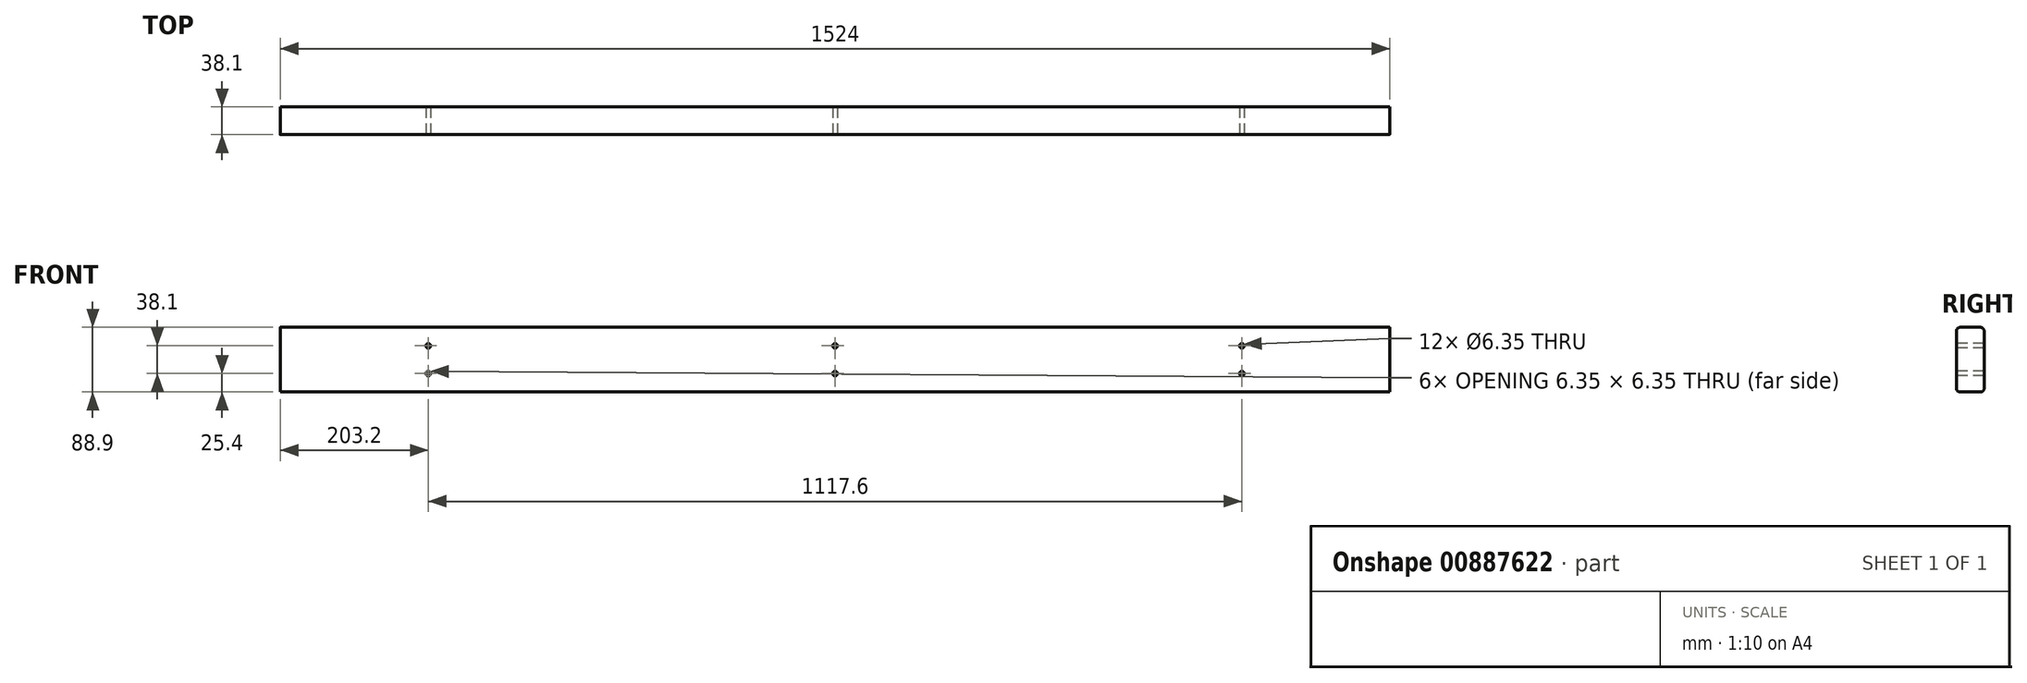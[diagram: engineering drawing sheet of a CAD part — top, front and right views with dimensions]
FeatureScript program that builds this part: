
annotation { "Feature Type Name" : "Feature", "Feature Type Description" : "" }
export const myFeature = defineFeature(function(context is Context, id is Id, definition is map)
    precondition{}
    {
        {
            var Q0;
            Q0=qCreatedBy(makeId("Right.planeOp"),FACE);
            var sketch = newSketch(context, id + "F0", { "sketchPlane" : qUnion([Q0])});
            skLineSegment(sketch, "E0.bottom", {"start": v(19.05, 44.45) * mm, "end": v(-19.05, 44.45) * mm});
            skLineSegment(sketch, "E0.top", {"start": v(19.05, -44.45) * mm, "end": v(-19.05, -44.45) * mm});
            skLineSegment(sketch, "E0.left", {"start": v(19.05, 44.45) * mm, "end": v(19.05, -44.45) * mm});
            skLineSegment(sketch, "E0.right", {"start": v(-19.05, 44.45) * mm, "end": v(-19.05, -44.45) * mm});
            skPoint(sketch, "E0.middle", {"position": v(0, 0) * mm});
            skSolve(sketch);
        }
        {
            var Q0;
            Q0=makeQuery(id+"F0.imprint","IMPRINT",FACE,{"disambiguationData":[TD([[makeQuery(id+"F0.imprint","IMPRINT",EDGE,{"derivedFrom":sQuery(id+"F0.wireOp",EDGE,"E0.bottom")}),1.0]])]});
            extrude(context, id + "F1", {"entities" : qUnion([Q0]), "endBound" : BoundingType.SYMMETRIC, "depth" : 1524 * mm, "offsetDistance" : 25.4 * mm});
        }
        {
            var Q0;
            Q0=makeQuery(id+"F1.opExtrude","SWEPT_FACE",FACE,{"disambiguationData":[OSD([sQuery(id+"F0.wireOp",EDGE,"E0.right")])]});
            var sketch = newSketch(context, id + "F2", { "sketchPlane" : qUnion([Q0])});
            skPoint(sketch, "E1", {"position": v(-558.8, 19.05) * mm});
            skPoint(sketch, "E2", {"position": v(-558.8, -19.05) * mm});
            skPoint(sketch, "E3", {"position": v(558.8, 19.05) * mm});
            skPoint(sketch, "E4", {"position": v(558.8, -19.05) * mm});
            skLineSegment(sketch, "E5", {"start": v(-762, 44.45) * mm, "end": v(-762, -44.45) * mm, "construction": true});
            skSolve(sketch);
        }
        {
            var Q0;
            Q0=sQuery(id+"F2.wireOp",VERTEX,"E1");
            var Q1;
            Q1=sQuery(id+"F2.wireOp",VERTEX,"E2");
            var Q2;
            Q2=sQuery(id+"F2.wireOp",VERTEX,"E4");
            var Q3;
            Q3=sQuery(id+"F2.wireOp",VERTEX,"E3");
            var Q4;
            Q4=makeQuery(id+"F1.opExtrude","SWEPT_BODY",BODY,{"disambiguationData":[OSD([sQuery(id+"F0.wireOp",EDGE,"E0.bottom"),sQuery(id+"F0.wireOp",EDGE,"E0.top"),sQuery(id+"F0.wireOp",EDGE,"E0.left"),sQuery(id+"F0.wireOp",EDGE,"E0.right")])]});
            hole(context, id + "F3", {"style" : HoleStyle.SIMPLE, "endStyle" : HoleEndStyle.THROUGH, "holeDiameter" : 6.35 * mm, "majorDiameter" : 6.35 * mm, "isTappedThrough" : true, "tappedDepth" : 12.7 * mm, "tapClearance" : 3, "locations" : qUnion([Q0, Q1, Q2, Q3]), "scope" : qUnion([Q4])});
        }
        {
            var Q0;
            Q0=makeQuery(id+"F1.opExtrude","SWEPT_EDGE",EDGE,{"disambiguationData":[OSD([sQuery(id+"F0.wireOp",EDGE,"E0.bottom"),sQuery(id+"F0.wireOp",EDGE,"E0.right")])]});
            var Q1;
            Q1=makeQuery(id+"F1.opExtrude","SWEPT_EDGE",EDGE,{"disambiguationData":[OSD([sQuery(id+"F0.wireOp",EDGE,"E0.bottom"),sQuery(id+"F0.wireOp",EDGE,"E0.left")])]});
            var Q2;
            Q2=makeQuery(id+"F1.opExtrude","SWEPT_EDGE",EDGE,{"disambiguationData":[OSD([sQuery(id+"F0.wireOp",EDGE,"E0.top"),sQuery(id+"F0.wireOp",EDGE,"E0.left")])]});
            var Q3;
            Q3=makeQuery(id+"F1.opExtrude","SWEPT_EDGE",EDGE,{"disambiguationData":[OSD([sQuery(id+"F0.wireOp",EDGE,"E0.top"),sQuery(id+"F0.wireOp",EDGE,"E0.right")])]});
            fillet(context, id + "F4", {"entities" : qUnion([Q0, Q1, Q2, Q3]), "radius" : 5.08 * mm, "tangentPropagation" : true, "allowEdgeOverflow" : false});
        }
        {
            var Q0;
            Q0=makeQuery(id+"F1.opExtrude","SWEPT_FACE",FACE,{"disambiguationData":[OSD([sQuery(id+"F0.wireOp",EDGE,"E0.right")])]});
            var sketch = newSketch(context, id + "F5", { "sketchPlane" : qUnion([Q0])});
            skPoint(sketch, "E6", {"position": v(0, 19.05) * mm});
            skPoint(sketch, "E7", {"position": v(0, -19.05) * mm});
            skSolve(sketch);
        }
        {
            var Q0;
            Q0=sQuery(id+"F5.wireOp",VERTEX,"E6");
            var Q1;
            Q1=sQuery(id+"F5.wireOp",VERTEX,"E7");
            var Q2;
            Q2=makeQuery(id+"F1.opExtrude","SWEPT_BODY",BODY,{"disambiguationData":[OSD([sQuery(id+"F0.wireOp",EDGE,"E0.bottom"),sQuery(id+"F0.wireOp",EDGE,"E0.top"),sQuery(id+"F0.wireOp",EDGE,"E0.left"),sQuery(id+"F0.wireOp",EDGE,"E0.right")])]});
            hole(context, id + "F6", {"style" : HoleStyle.SIMPLE, "endStyle" : HoleEndStyle.THROUGH, "holeDiameter" : 6.35 * mm, "majorDiameter" : 6.35 * mm, "isTappedThrough" : true, "tappedDepth" : 12.7 * mm, "tapClearance" : 3, "locations" : qUnion([Q0, Q1]), "scope" : qUnion([Q2])});
        }
    });
